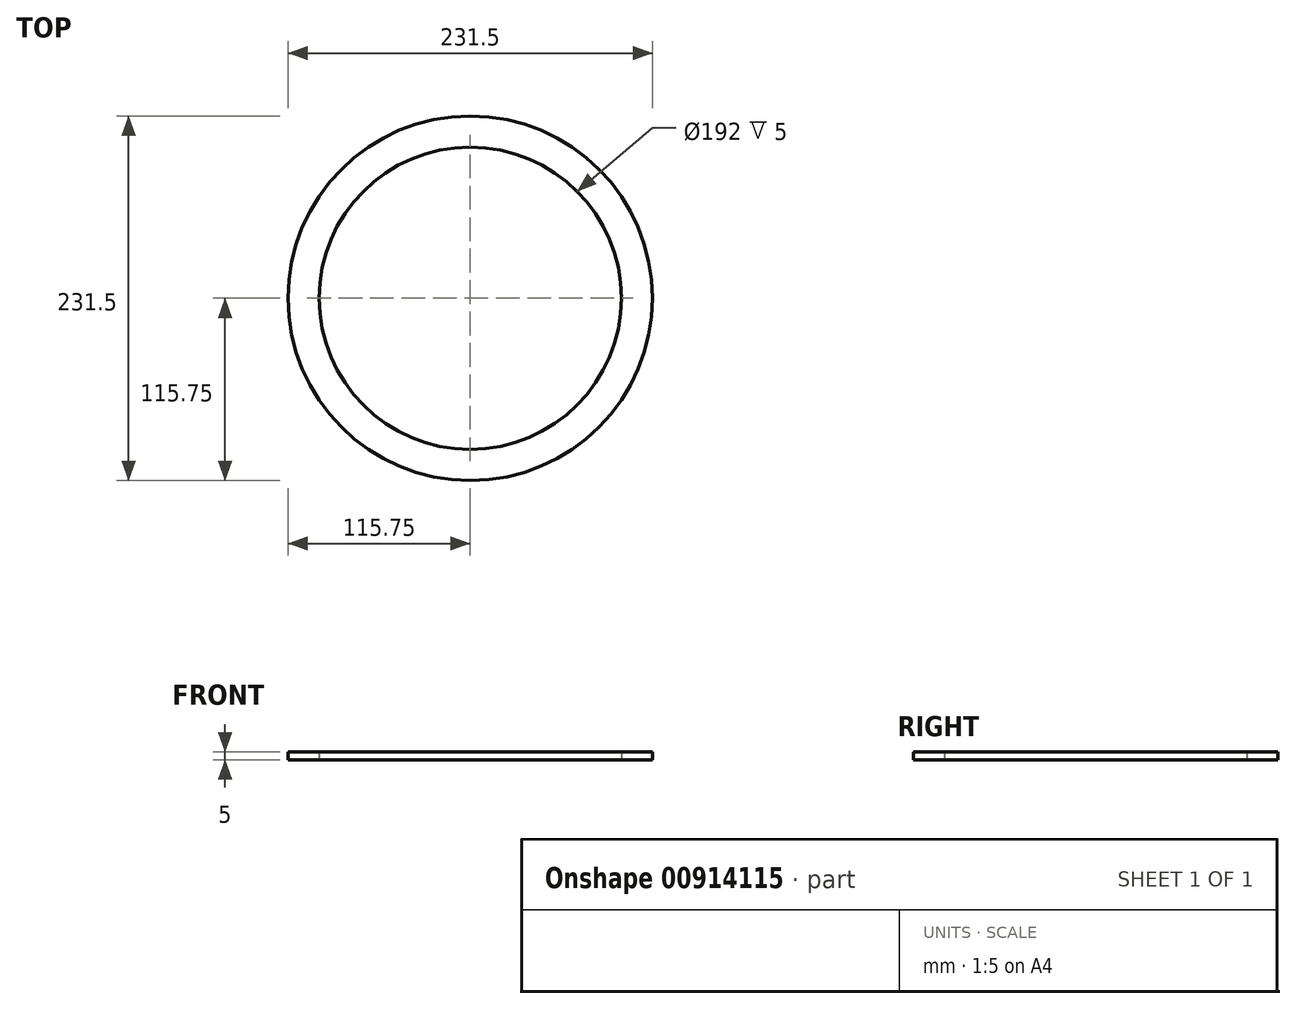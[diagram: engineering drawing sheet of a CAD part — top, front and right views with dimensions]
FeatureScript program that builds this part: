
annotation { "Feature Type Name" : "Feature", "Feature Type Description" : "" }
export const myFeature = defineFeature(function(context is Context, id is Id, definition is map)
    precondition{}
    {
        {
            var Q0;
            Q0=qCreatedBy(makeId("Top.planeOp"),FACE);
            var sketch = newSketch(context, id + "F0", { "sketchPlane" : qUnion([Q0])});
            skCircle(sketch, "E0", {"center": v(0, 0) * mm, "radius": 96 * mm});
            skCircle(sketch, "E1", {"center": v(0, 0) * mm, "radius": 115.75 * mm});
            skSolve(sketch);
        }
        {
            var Q0;
            Q0=makeQuery(id+"F0.imprint","IMPRINT",FACE,{"disambiguationData":[TD([[makeQuery(id+"F0.imprint","IMPRINT",EDGE,{"derivedFrom":sQuery(id+"F0.wireOp",EDGE,"E0")}),-1.0]])]});
            extrude(context, id + "F1", {"entities" : qUnion([Q0]), "depth" : 5 * mm, "offsetDistance" : 25 * mm});
        }
    });
